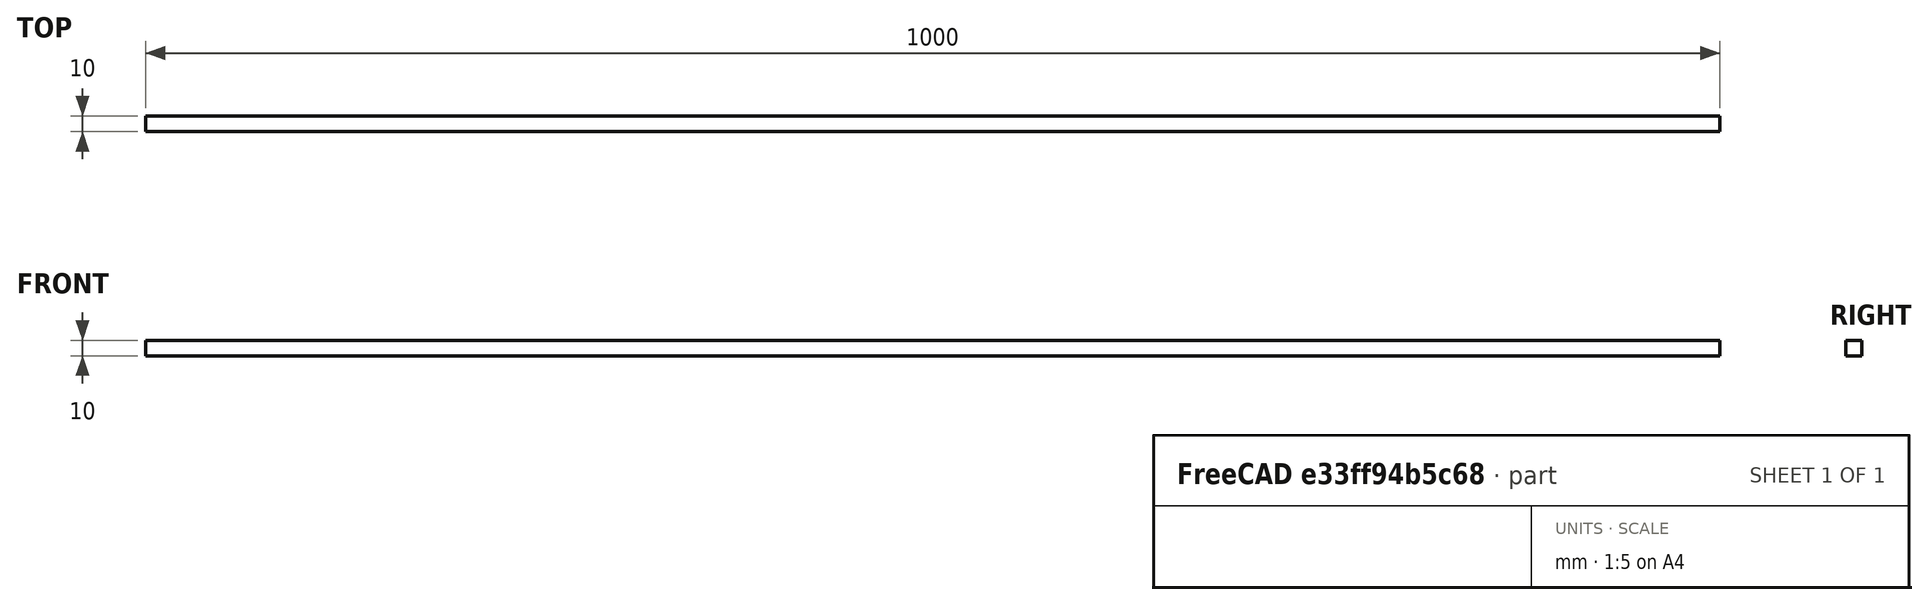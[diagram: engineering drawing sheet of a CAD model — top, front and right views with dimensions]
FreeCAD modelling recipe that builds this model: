
FCSTD DOCUMENT  (FreeCAD 0.21R33694 (Git))
Label: Elastica_2
License: All rights reserved
LicenseURL: http://en.wikipedia.org/wiki/All_rights_reserved
objects: Fem::ConstraintDisplacement×2, Sketcher::SketchObject×1, Fem::FemSolverObjectPython×1, Part::Extrusion×1, Fem::ConstraintForce×1, Fem::ConstraintFixed×1, Fem::FemMeshObjectPython×1, App::MaterialObjectPython×1, Fem::FemAnalysis×1
note: 2 computed .brp shape members not serialized (recipe doc carries the construction recipe); baked Part::Feature solids carry a one-line shape summary decoded from their .brp

FEATURE [Sketcher::SketchObject] Sketch
  FullyConstrained = true
  Placement = pos=(0,0,0) rot=(1,0,0;1.5708rad)
  sketch-geometry (6):
    g0: LineSegment StartX=500 StartY=10 StartZ=0 EndX=1000 EndY=10 EndZ=0
    g1: LineSegment StartX=1000 StartY=10 StartZ=0 EndX=1000 EndY=0 EndZ=0
    g2: LineSegment StartX=1000 StartY=0 StartZ=0 EndX=500 EndY=0 EndZ=0
    g3: LineSegment StartX=0 StartY=0 StartZ=0 EndX=500 EndY=0 EndZ=0
    g4: LineSegment StartX=0 StartY=10 StartZ=0 EndX=500 EndY=10 EndZ=0
    g5: LineSegment StartX=0 StartY=10 StartZ=0 EndX=0 EndY=0 EndZ=0
  constraints (17):
    c: PointOnObject(g4,g-2)
    c: Coincident(g0,g1)
    c: Vertical(g1)
    c: Coincident(g1,g2)
    c: DistanceY(g-1,g4) = 10
    c: DistanceY(g1,g1) = 10
    c: DistanceY(g2,g0) = 10
    c: PointOnObject(g1,g-1)
    c: DistanceX(g-1,g1) = 1000
    c: DistanceY(g-1,g2) = 0
    c: DistanceX(g-1,g2) = 500
    c: DistanceX(g4,g0) = 500
    c: Coincident(g4,g0)
    c: Coincident(g2,g3)
    c: Coincident(g-1,g3)
    c: Coincident(g5,g4)
    c: Coincident(g5,g3)
FEATURE [Fem::FemSolverObjectPython] SolverCcxTools  # FEM object (typed FeaturePython)
  AnalysisType = 0
  BeamShellResultOutput3D = false
  BucklingFactors = 1
  EigenmodeHighLimit = 1000000
  EigenmodeLowLimit = 0
  EigenmodesCount = 10
  GeometricalNonlinearity = 0
  IterationsControlParameterCutb = 0.25,0.5,0.75,0.85,,,1.5,
  IterationsControlParameterIter = 4,8,9,200,10,400,,200,,
  IterationsControlParameterTimeUse = false
  IterationsThermoMechMaximum = 2000
  IterationsUserDefinedIncrementations = false
  IterationsUserDefinedTimeStepLength = false
  MaterialNonlinearity = 0
  MatrixSolverType = 0
  SplitInputWriter = false
  ThermoMechSteadyState = true
  TimeEnd = 1
  TimeInitialStep = 0.01
FEATURE [Part::Extrusion] Extrude
  Base = -> Sketch
  Dir = (0,-1,2e-16)
  DirMode = 2
  FaceMakerClass = Part::FaceMakerBullseye
  LengthFwd = 10
  LengthRev = 0
  Solid = true
  Symmetric = false
FEATURE [Fem::ConstraintDisplacement] ConstraintDisplacement
  NormalDirection = (0,0,1)
  Normals = (2) [(0,0,1),(0,0,1)]
  Points = (2) [(0,0,0),(0,-10,2.2e-15)]
  References = -> [Extrude]
  hasXFormula = false
  hasYFormula = false
  hasZFormula = false
  rotxFix = false
  rotxFree = true
  rotyFix = false
  rotyFree = true
  rotzFix = false
  rotzFree = true
  useFlowSurfaceForce = false
  xDisplacement = 0
  xFix = false
  xFree = true
  xRotation = 0
  yDisplacement = 0
  yFix = false
  yFree = true
  yRotation = 0
  zDisplacement = 0
  zFix = false
  zFree = false
  zRotation = 0
FEATURE [Fem::ConstraintForce] ConstraintForce
  DirectionVector = (1,0,0)
  Force = 1000
  NormalDirection = (-1,0,0)
  Points = (9) [(0,-10,10),(0,-10,5),(0,-10,1.77636e-15),(0,-5,10),(0,-5,5),(0,-5,1.77636e-15),(0,2.22e-15,10),(0,1.12e-15,5),(0,2e-17,0)]
  References = -> [Extrude]
  Reversed = true
FEATURE [Fem::ConstraintDisplacement] ConstraintDisplacement001
  NormalDirection = (0,-1,2e-16)
  Normals = (15) [(0,-1,2.2e-16),(0,-1,2.2e-16),(0,-1,2.2e-16),(0,-1,2.2e-16),(0,-1,2.2e-16),(0,-1,2.2e-16),(0,-1,2.2e-16),(0,-1,2.2e-16),(0,-1,2.2e-16),(0,-1,2.2e-16),+5 more]
  Points = (15) [(0,-10,2e-15),(0,-10,5),(0,-10,10),(250,-10,2e-15),(250,-10,5),(250,-10,10),(500,-10,2e-15),(500,-10,5),(500,-10,10),(750,-10,2e-15),(750,-10,5),+4 more]
  References = -> [Extrude]
  hasXFormula = false
  hasYFormula = false
  hasZFormula = false
  rotxFix = false
  rotxFree = true
  rotyFix = false
  rotyFree = true
  rotzFix = false
  rotzFree = true
  useFlowSurfaceForce = false
  xDisplacement = 0
  xFix = false
  xFree = true
  xRotation = 0
  yDisplacement = 0
  yFix = false
  yFree = false
  yRotation = 0
  zDisplacement = 0
  zFix = false
  zFree = true
  zRotation = 0
FEATURE [Fem::ConstraintFixed] ConstraintFixed
  NormalDirection = (1,0,0)
  Normals = (9) [(1,0,0),(1,0,0),(1,0,0),(1,0,0),(1,0,0),(1,0,0),(1,0,0),(1,0,0),(1,0,0)]
  Points = (9) [(1000,-10,10),(1000,-10,5),(1000,-10,1.77636e-15),(1000,-5,10),(1000,-5,5),(1000,-5,1.77636e-15),(1000,2.22e-15,10),(1000,1.12e-15,5),(1000,2e-17,0)]
  References = -> [Extrude]
FEATURE [Fem::FemMeshObjectPython] FEMMeshGmsh  # FEM object (typed FeaturePython)
  Algorithm2D = 0
  Algorithm3D = 0
  CharacteristicLengthMax = 50
  CharacteristicLengthMin = 0
  CoherenceMesh = true
  ElementDimension = 0
  ElementOrder = 1
  GeometryTolerance = 1e-06
  GroupsOfNodes = false
  HighOrderOptimize = 0
  MeshSizeFromCurvature = 12
  OptimizeNetgen = false
  OptimizeStd = true
  Part = -> Extrude
  RecombinationAlgorithm = 0
  Recombine3DAll = false
  RecombineAll = false
  SecondOrderLinear = false
FEATURE [App::MaterialObjectPython] MaterialSolid  # material (typed FeaturePython)
  Category = 0
  Material = AuthorAndLicense=(c) 2014 M. Münch - GNU Lesser General Public License (LGPL),CardName=Steel-St-E-315,Density=7800 kg/m^3,Father=Metal,+13 more (map truncated)
FEATURE [Fem::FemAnalysis] Analysis
  Group = -> [ConstraintDisplacement,ConstraintForce,SolverCcxTools,ConstraintDisplacement001,ConstraintFixed,FEMMeshGmsh,MaterialSolid]
